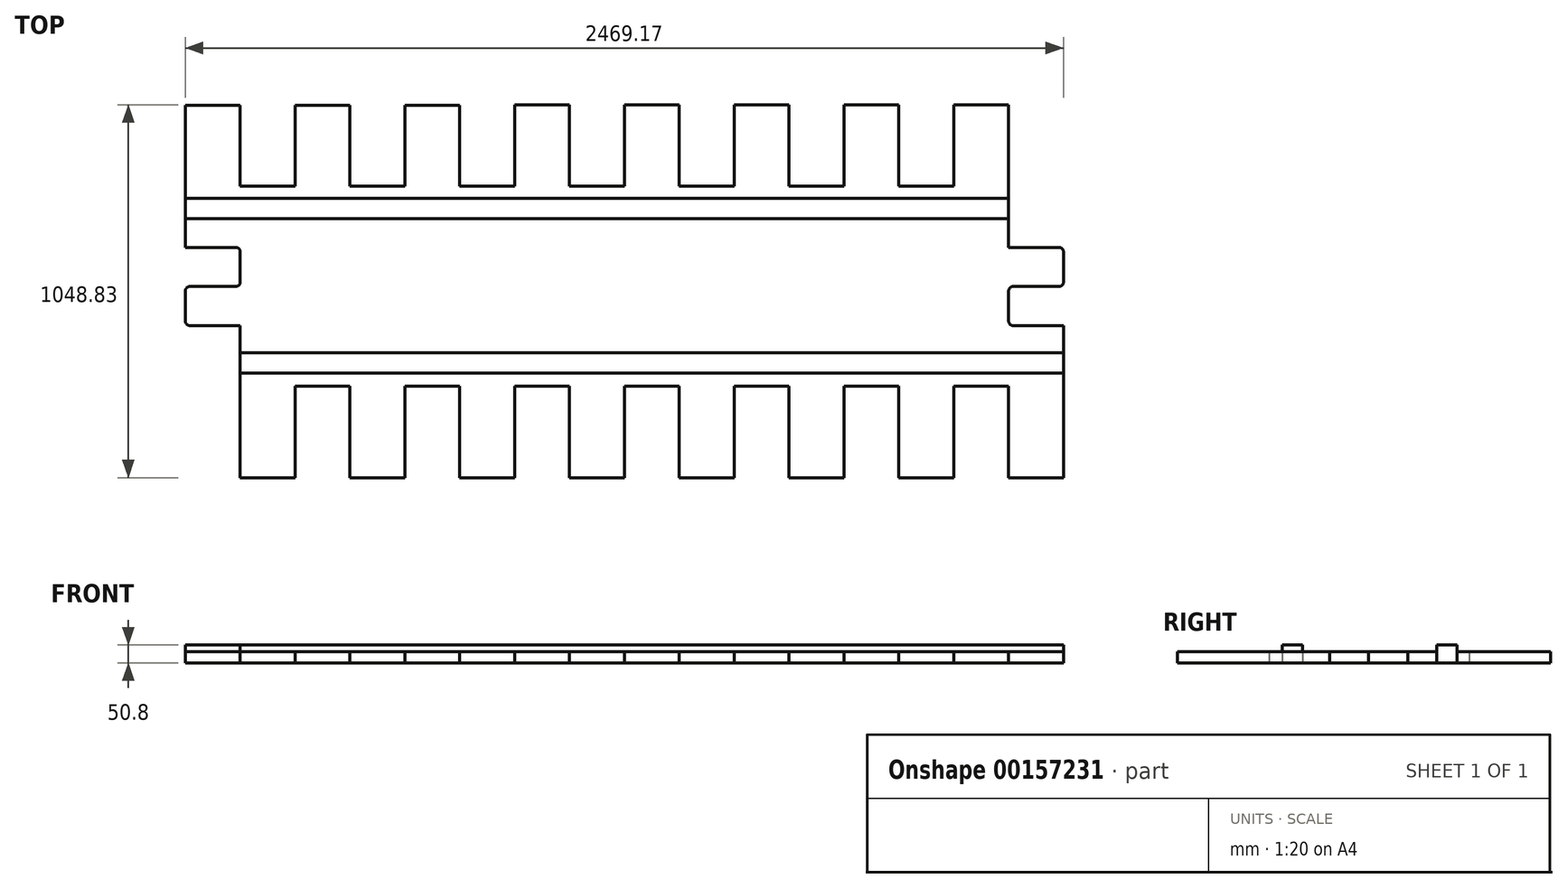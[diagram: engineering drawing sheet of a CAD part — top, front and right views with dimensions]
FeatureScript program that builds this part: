
annotation { "Feature Type Name" : "Feature", "Feature Type Description" : "" }
export const myFeature = defineFeature(function(context is Context, id is Id, definition is map)
    precondition{}
    {
        {
            var Q0;
            Q0=qCreatedBy(makeId("Top.planeOp"),FACE);
            var sketch = newSketch(context, id + "F0", { "sketchPlane" : qUnion([Q0])});
            skLineSegment(sketch, "E0", {"start": v(0, 0) * mm, "end": v(141.6, 0) * mm});
            skLineSegment(sketch, "E1", {"start": v(154.3, -12.7) * mm, "end": v(154.3, -97.3) * mm});
            skLineSegment(sketch, "E2", {"start": v(141.6, -110) * mm, "end": v(12.7, -110) * mm});
            skLineSegment(sketch, "E3", {"start": v(0, -122.7) * mm, "end": v(0, -207.32) * mm});
            skLineSegment(sketch, "E4", {"start": v(12.7, -220.02) * mm, "end": v(154.3, -220.02) * mm});
            skLineSegment(sketch, "E5", {"start": v(154.3, -220.02) * mm, "end": v(154.3, -647.87) * mm});
            skLineSegment(sketch, "E6", {"start": v(154.3, -647.87) * mm, "end": v(0, -647.87) * mm});
            skLineSegment(sketch, "E7", {"start": v(0, -647.87) * mm, "end": v(0, -389.82) * mm});
            skLineSegment(sketch, "E8", {"start": v(0, -389.82) * mm, "end": v(-154.3, -389.82) * mm});
            skLineSegment(sketch, "E9", {"start": v(-154.3, -389.82) * mm, "end": v(-154.3, -647.87) * mm});
            skLineSegment(sketch, "E10", {"start": v(-154.3, -647.87) * mm, "end": v(-308.61, -647.87) * mm});
            skLineSegment(sketch, "E11", {"start": v(-308.61, -647.87) * mm, "end": v(-308.61, -389.82) * mm});
            skLineSegment(sketch, "E12", {"start": v(-308.61, -389.82) * mm, "end": v(-462.92, -389.82) * mm});
            skLineSegment(sketch, "E13", {"start": v(-462.92, -389.82) * mm, "end": v(-462.92, -647.87) * mm});
            skLineSegment(sketch, "E14", {"start": v(-462.92, -647.87) * mm, "end": v(-617.22, -647.87) * mm});
            skLineSegment(sketch, "E15", {"start": v(-617.22, -647.87) * mm, "end": v(-617.22, -389.82) * mm});
            skLineSegment(sketch, "E16", {"start": v(-617.22, -389.82) * mm, "end": v(-771.53, -389.82) * mm});
            skLineSegment(sketch, "E17", {"start": v(-771.53, -389.82) * mm, "end": v(-771.53, -647.87) * mm});
            skLineSegment(sketch, "E18", {"start": v(-771.53, -647.87) * mm, "end": v(-925.83, -647.87) * mm});
            skLineSegment(sketch, "E19", {"start": v(-925.83, -647.87) * mm, "end": v(-925.83, -389.82) * mm});
            skPoint(sketch, "E20.visualSharp", {"position": v(154.3, 0) * mm});
            skArc(sketch, "E20.filletArc", {"start": v(154.3, -12.7) * mm, "mid": v(150.59, -3.72) * mm, "end": v(141.6, 0) * mm});
            skPoint(sketch, "E21.visualSharp", {"position": v(154.3, -110) * mm});
            skArc(sketch, "E21.filletArc", {"start": v(141.6, -110) * mm, "mid": v(150.59, -106.29) * mm, "end": v(154.3, -97.3) * mm});
            skPoint(sketch, "E22.visualSharp", {"position": v(0, -220.02) * mm});
            skArc(sketch, "E22.filletArc", {"start": v(0, -207.32) * mm, "mid": v(3.72, -216.3) * mm, "end": v(12.7, -220.02) * mm});
            skPoint(sketch, "E23.visualSharp", {"position": v(0, -110) * mm});
            skArc(sketch, "E23.filletArc", {"start": v(12.7, -110) * mm, "mid": v(3.72, -113.73) * mm, "end": v(0, -122.7) * mm});
            skLineSegment(sketch, "E24", {"start": v(-925.83, -389.82) * mm, "end": v(-1080.14, -389.82) * mm});
            skLineSegment(sketch, "E25", {"start": v(-1080.14, -389.82) * mm, "end": v(-1080.14, -647.87) * mm});
            skLineSegment(sketch, "E26", {"start": v(-1080.14, -647.87) * mm, "end": v(-1234.44, -647.87) * mm});
            skLineSegment(sketch, "E27", {"start": v(-1234.44, -647.87) * mm, "end": v(-1234.44, -389.82) * mm});
            skLineSegment(sketch, "E28", {"start": v(-1234.44, -389.82) * mm, "end": v(-1388.75, -389.82) * mm});
            skLineSegment(sketch, "E29", {"start": v(-1388.75, -389.82) * mm, "end": v(-1388.75, -647.87) * mm});
            skLineSegment(sketch, "E30", {"start": v(-1388.75, -647.87) * mm, "end": v(-1543.05, -647.87) * mm});
            skLineSegment(sketch, "E31", {"start": v(-1543.05, -647.87) * mm, "end": v(-1543.05, -389.82) * mm});
            skLineSegment(sketch, "E32", {"start": v(-1543.05, -389.82) * mm, "end": v(-1697.36, -389.82) * mm});
            skLineSegment(sketch, "E33", {"start": v(-1697.36, -389.82) * mm, "end": v(-1697.36, -647.87) * mm});
            skLineSegment(sketch, "E34", {"start": v(-1697.36, -647.87) * mm, "end": v(-1851.67, -647.87) * mm});
            skLineSegment(sketch, "E35", {"start": v(-1851.67, -647.87) * mm, "end": v(-1851.67, -389.82) * mm});
            skLineSegment(sketch, "E36", {"start": v(-1851.67, -389.82) * mm, "end": v(-2005.97, -389.82) * mm});
            skLineSegment(sketch, "E37", {"start": v(-2005.97, -389.82) * mm, "end": v(-2005.97, -647.87) * mm});
            skLineSegment(sketch, "E38", {"start": v(-2005.97, -647.87) * mm, "end": v(-2160.29, -647.87) * mm});
            skLineSegment(sketch, "E39", {"start": v(-2160.29, -647.87) * mm, "end": v(-2160.29, -220.02) * mm});
            skLineSegment(sketch, "E40", {"start": v(-2160.29, -220.02) * mm, "end": v(-2301.9, -220.02) * mm});
            skLineSegment(sketch, "E41", {"start": v(-2314.6, -207.32) * mm, "end": v(-2314.6, -122.7) * mm});
            skLineSegment(sketch, "E42", {"start": v(-2301.9, -110) * mm, "end": v(-2172.99, -110) * mm});
            skLineSegment(sketch, "E43", {"start": v(-2160.29, -97.3) * mm, "end": v(-2160.29, -12.7) * mm});
            skLineSegment(sketch, "E44", {"start": v(-2172.99, 0) * mm, "end": v(-2314.6, 0) * mm});
            skLineSegment(sketch, "E45", {"start": v(-2314.6, 0) * mm, "end": v(-2314.6, 399.88) * mm});
            skPoint(sketch, "E46.visualSharp", {"position": v(-2314.6, -110) * mm});
            skArc(sketch, "E46.filletArc", {"start": v(-2301.9, -110) * mm, "mid": v(-2310.87, -113.73) * mm, "end": v(-2314.6, -122.7) * mm});
            skPoint(sketch, "E47.visualSharp", {"position": v(-2314.6, -220.02) * mm});
            skArc(sketch, "E47.filletArc", {"start": v(-2314.6, -207.32) * mm, "mid": v(-2310.87, -216.3) * mm, "end": v(-2301.9, -220.02) * mm});
            skPoint(sketch, "E48.visualSharp", {"position": v(-2160.29, -110) * mm});
            skArc(sketch, "E48.filletArc", {"start": v(-2172.99, -110) * mm, "mid": v(-2164, -106.29) * mm, "end": v(-2160.29, -97.3) * mm});
            skPoint(sketch, "E49.visualSharp", {"position": v(-2160.29, 0) * mm});
            skArc(sketch, "E49.filletArc", {"start": v(-2160.29, -12.7) * mm, "mid": v(-2164, -3.72) * mm, "end": v(-2172.99, 0) * mm});
            skLineSegment(sketch, "E50", {"start": v(-2314.6, 399.88) * mm, "end": v(-2160.29, 399.88) * mm});
            skLineSegment(sketch, "E51", {"start": v(-2160.29, 399.88) * mm, "end": v(-2160.29, 172.14) * mm});
            skLineSegment(sketch, "E52", {"start": v(-2160.29, 172.14) * mm, "end": v(-2005.98, 172.14) * mm});
            skLineSegment(sketch, "E53", {"start": v(-2005.98, 172.14) * mm, "end": v(-2005.98, 399.88) * mm});
            skLineSegment(sketch, "E54", {"start": v(-2005.98, 399.88) * mm, "end": v(-1851.68, 399.88) * mm});
            skLineSegment(sketch, "E55", {"start": v(-1851.68, 399.88) * mm, "end": v(-1851.68, 172.14) * mm});
            skLineSegment(sketch, "E56", {"start": v(-1851.68, 172.14) * mm, "end": v(-1697.37, 172.14) * mm});
            skLineSegment(sketch, "E57", {"start": v(-1697.37, 172.14) * mm, "end": v(-1697.37, 399.88) * mm});
            skLineSegment(sketch, "E58", {"start": v(-1697.37, 399.88) * mm, "end": v(-1543.07, 399.88) * mm});
            skLineSegment(sketch, "E59", {"start": v(-1543.07, 399.88) * mm, "end": v(-1543.07, 172.14) * mm});
            skLineSegment(sketch, "E60", {"start": v(-1543.07, 172.14) * mm, "end": v(-1388.76, 172.14) * mm});
            skLineSegment(sketch, "E61", {"start": v(-1388.76, 172.14) * mm, "end": v(-1388.76, 400.96) * mm});
            skLineSegment(sketch, "E62", {"start": v(-1388.76, 400.96) * mm, "end": v(-1234.46, 400.96) * mm});
            skLineSegment(sketch, "E63", {"start": v(-1234.46, 400.96) * mm, "end": v(-1234.46, 172.14) * mm});
            skLineSegment(sketch, "E64", {"start": v(-1234.46, 172.14) * mm, "end": v(-1080.15, 172.14) * mm});
            skLineSegment(sketch, "E65", {"start": v(-1080.15, 172.14) * mm, "end": v(-1080.15, 400.96) * mm});
            skLineSegment(sketch, "E66", {"start": v(-1080.15, 400.96) * mm, "end": v(-925.85, 400.96) * mm});
            skLineSegment(sketch, "E67", {"start": v(-925.85, 400.96) * mm, "end": v(-925.85, 172.14) * mm});
            skLineSegment(sketch, "E68", {"start": v(-925.85, 172.14) * mm, "end": v(-771.54, 172.14) * mm});
            skLineSegment(sketch, "E69", {"start": v(-771.54, 172.14) * mm, "end": v(-771.54, 400.96) * mm});
            skLineSegment(sketch, "E70", {"start": v(-771.54, 400.96) * mm, "end": v(-617.24, 400.96) * mm});
            skLineSegment(sketch, "E71", {"start": v(-617.24, 400.96) * mm, "end": v(-617.24, 172.14) * mm});
            skLineSegment(sketch, "E72", {"start": v(-617.24, 172.14) * mm, "end": v(-462.93, 172.14) * mm});
            skLineSegment(sketch, "E73", {"start": v(-462.93, 172.14) * mm, "end": v(-462.93, 400.96) * mm});
            skLineSegment(sketch, "E74", {"start": v(-462.93, 400.96) * mm, "end": v(-308.63, 400.96) * mm});
            skLineSegment(sketch, "E75", {"start": v(-308.63, 400.96) * mm, "end": v(-308.63, 172.14) * mm});
            skLineSegment(sketch, "E76", {"start": v(-308.63, 172.14) * mm, "end": v(-154.32, 172.14) * mm});
            skLineSegment(sketch, "E77", {"start": v(-154.32, 172.14) * mm, "end": v(-154.32, 400.96) * mm});
            skLineSegment(sketch, "E78", {"start": v(-154.32, 400.96) * mm, "end": v(-0.02, 400.96) * mm});
            skLineSegment(sketch, "E79", {"start": v(-0.02, 400.96) * mm, "end": v(-0.02, 172.14) * mm});
            skLineSegment(sketch, "E80", {"start": v(-0.02, 172.14) * mm, "end": v(0, 0) * mm});
            skSolve(sketch);
        }
        {
            var Q0;
            Q0=makeQuery(id+"F0.imprint","IMPRINT",FACE,{"disambiguationData":[TD([[makeQuery(id+"F0.imprint","IMPRINT",EDGE,{"derivedFrom":sQuery(id+"F0.wireOp",EDGE,"E0")}),-1.0]])]});
            var sketch = newSketch(context, id + "F1", { "sketchPlane" : qUnion([Q0])});
            skLineSegment(sketch, "E81", {"start": v(-2314.86, 138.26) * mm, "end": v(0, 138.26) * mm});
            skLineSegment(sketch, "E82.0", {"start": v(-2314.86, 81.11) * mm, "end": v(0, 81.11) * mm});
            skLineSegment(sketch, "E83", {"start": v(-2160.59, -353.29) * mm, "end": v(154.12, -353.29) * mm});
            skLineSegment(sketch, "E84.0", {"start": v(-2160.59, -296.14) * mm, "end": v(154.12, -296.14) * mm});
            skLineSegment(sketch, "E85", {"start": v(-2314.86, 138.26) * mm, "end": v(-2314.86, 81.11) * mm});
            skLineSegment(sketch, "E86", {"start": v(-2160.59, -296.14) * mm, "end": v(-2160.59, -353.29) * mm});
            skLineSegment(sketch, "E87", {"start": v(154.12, -296.14) * mm, "end": v(154.12, -353.29) * mm});
            skLineSegment(sketch, "E88", {"start": v(0, 138.26) * mm, "end": v(0, 81.11) * mm});
            skSolve(sketch);
        }
        {
            var Q0;
            Q0 = qSketchRegion(id + "F0", true);
            extrude(context, id + "F2", {"entities" : qUnion([Q0]), "depth" : 31.75 * mm});
        }
        {
            var Q0;
            Q0 = qSketchRegion(id + "F1", true);
            extrude(context, id + "F3", {"entities" : qUnion([Q0]), "operationType" : NewBodyOperationType.ADD, "depth" : 50.8 * mm});
        }
    });
